# Revit family: Security_PowerSupply_AiPhone_IS-PU-UL
name_source: partatom
category: Electrical Fixtures
units: mm (PartAtom-declared; Revit-internal decimal feet)

## family parameters
Always vertical = No
Classification Number = 23.85.30.11.27
Cut with Voids When Loaded = No
Maintain Annotation Orientation = No
Part Type = Normal
Room Calculation Point = No
Round Connector Dimension = Use Diameter
Shared = No
Work Plane-Based = Yes

## types (2) — shared parameters
Assembly Code = D5030900
Construction Details = http://www.arcat.com
Default Elevation = 0' - 0"
Description = Aiphone IS Series Power Supply
Electrical_Wattage = 120 W
Green Building-LEED = http://www.arcat.com
Installation-Fabrication = http://www.aiphone.com
Keynote = 13700
Manufacturer = Aiphone Corp.
Manufacturer Fax = 425-455-0071
Manufacturer Website = http://www.aiphone.com
Material = Metal - Steel - Aiphone - Painted - Black
Model = IS-PU-UL
Operating Temperature Range = 32 - 140 F
Product Data = http://www.arcat.com
Product Properties = http://arcat.com
Revision = R1_2015-05
Sales Information = http://www.aiphone.com
Send Message = http://www.arcat.com
Specification = http://arcat.com
Supplied Amperage = 2 A
URL = http://www.aiphone.com
Unit Depth = 0' - 5 5/16"
Unit Height = 0' - 10 7/16"
Unit Width = 0' - 5 1/8"
zero-valued in all types: Expected Lifespan (Years), Maintenance Schedule (Months), Warranty Duration (Years)

## per-type parameters (varying)
| type | Electrical_Frequency |
| 100-240V 50Hz | 50 Hz |
| 100-240V 60Hz | 60 Hz |

## geometry (parser evidence)
native form markers: Sweep x2
no freeform markers — native parametric forms only
